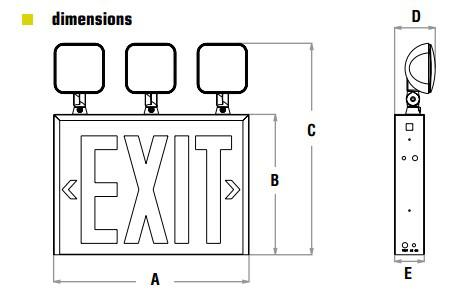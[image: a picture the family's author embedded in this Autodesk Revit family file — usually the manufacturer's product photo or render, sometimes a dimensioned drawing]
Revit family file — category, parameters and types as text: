
# Revit family: NYC STX CLRU3WHT
name_source: partatom
category: Lighting Fixtures
units: mm (PartAtom-declared; Revit-internal decimal feet)

## family parameters
Always vertical = Yes
Cut with Voids When Loaded = No
Host = Wall
Light Source = Yes
Maintain Annotation Orientation = No
Part Type = Normal
Room Calculation Point = No
Round Connector Dimension = Use Diameter
Shared = No

## types (1)
- NYC STX CLRU3WHT
    Color Filter = 16777215
    Default Elevation = 0.00"
    Dimming Lamp Color Temperature Shift = <None>
    Emit from Line Length = 24.00"
    HOUSING MATERIAL = HOUSING MATERIAL
    LENS MATERIAL = LENS MATERIAL
    LETTER MATERIAL = LETTERS MATERIAL RED
    Lamp = LED
    MOUNTING HEIGHT = 90.00"
    Manufacturer = BEGHELLI
    Model = NYC STX CLRU3WHT
    Photometric Web File = NYC-EST NYC-STX-C BEST ITL68902 - 12 LED SQ head (1).IES
    Tilt Angle = 90.00°
    Type Image = NYC STX C - IMAGE.jpg
    Wattage Comments = 4.5W

## geometry (parser evidence)
native form markers: Sweep x29
no freeform markers — native parametric forms only
